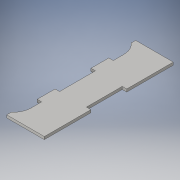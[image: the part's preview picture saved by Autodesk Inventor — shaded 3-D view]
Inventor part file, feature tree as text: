
AUTODESK INVENTOR PART (.ipt)
format: ipt  version: 2016 (Build 200138000, 138)  size: 133,120 bytes
history: native  units: mm
features: other x1, extrude x1, sketch x1
ambient origin geometry x8: Origin, YZ Plane, XZ Plane, XY Plane, X Axis, Y Axis, Z Axis, Center Point
bodies: Solid1 (feature_tree)
feature tree (3):
  other  "<userpath>\Documents\GitHub\3D\Hoja Oculta\Parametros.xlsx"
  extrude  "Cuerpo"  Depth=30.0mm
  sketch  "Sketch2"  dims[d0=144.0mm d1=30.0mm d2=5.0mm d3=7.0mm d4=20.0mm d5=7.0mm d6=5.0mm d9=20.0mm d10=5.0mm d11=5.0mm d12=40.0mm d13=40.0mm d14=5.0mm d15=5.0mm d16=20.0mm d17=20.0mm d18=3.0mm d19=0.0mm]
